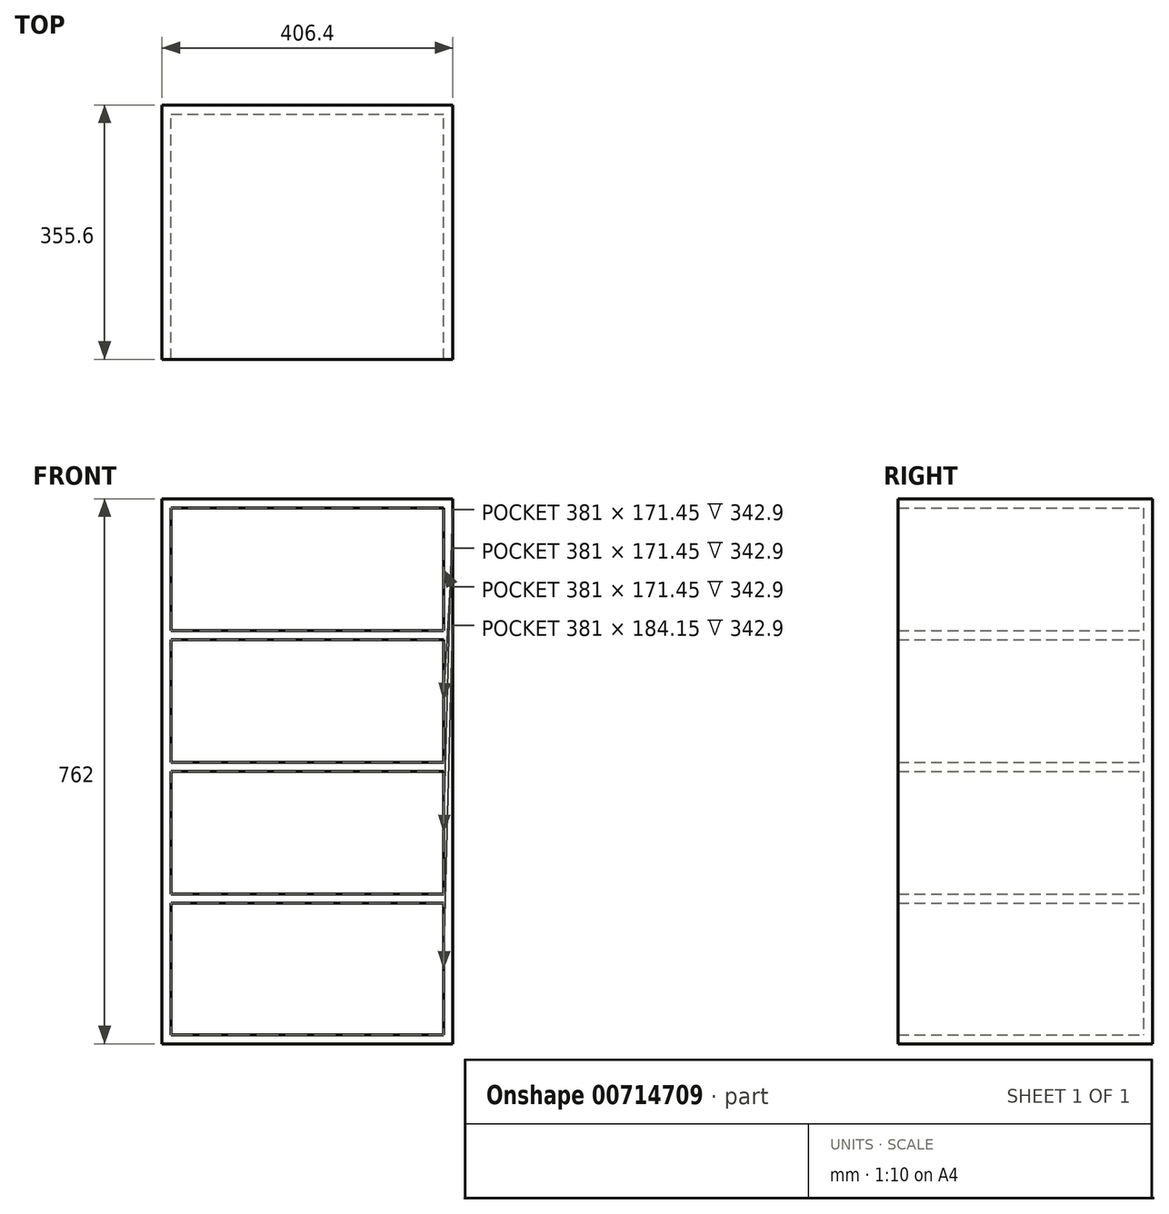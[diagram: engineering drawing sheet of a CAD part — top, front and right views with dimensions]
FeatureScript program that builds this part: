
annotation { "Feature Type Name" : "Feature", "Feature Type Description" : "" }
export const myFeature = defineFeature(function(context is Context, id is Id, definition is map)
    precondition{}
    {
        {
            var Q0;
            Q0=qCreatedBy(makeId("Front.planeOp"),FACE);
            var sketch = newSketch(context, id + "F0", { "sketchPlane" : qUnion([Q0])});
            skLineSegment(sketch, "E0.bottom", {"start": v(203.2, 381) * mm, "end": v(-203.2, 381) * mm});
            skLineSegment(sketch, "E0.top", {"start": v(203.2, -381) * mm, "end": v(-203.2, -381) * mm});
            skLineSegment(sketch, "E0.left", {"start": v(203.2, 381) * mm, "end": v(203.2, -381) * mm});
            skLineSegment(sketch, "E0.right", {"start": v(-203.2, 381) * mm, "end": v(-203.2, -381) * mm});
            skPoint(sketch, "E0.middle", {"position": v(0, 0) * mm});
            skSolve(sketch);
        }
        {
            var Q0;
            Q0 = qSketchRegion(id + "F0", true);
            extrude(context, id + "F1", {"entities" : qUnion([Q0]), "depth" : 355.6 * mm, "offsetDistance" : 25.4 * mm});
        }
        {
            var Q0;
            Q0=makeQuery(id+"F1.opExtrude","CAP_FACE",FACE,{"disambiguationData":[OSD([sQuery(id+"F0.wireOp",EDGE,"E0.bottom"),sQuery(id+"F0.wireOp",EDGE,"E0.top"),sQuery(id+"F0.wireOp",EDGE,"E0.left"),sQuery(id+"F0.wireOp",EDGE,"E0.right")])],"isStart":false});
            shell(context, id + "F2", {"entities" : qUnion([Q0]), "thickness" : 12.7 * mm});
        }
        {
            var Q0;
            Q0=makeQuery(id+"F2.opShell","OFFSET_FACE",FACE,{"disambiguationData":[OSD([sQuery(id+"F0.wireOp",EDGE,"E0.bottom"),sQuery(id+"F0.wireOp",EDGE,"E0.top"),sQuery(id+"F0.wireOp",EDGE,"E0.left"),sQuery(id+"F0.wireOp",EDGE,"E0.right")])]});
            var sketch = newSketch(context, id + "F3", { "sketchPlane" : qUnion([Q0])});
            skLineSegment(sketch, "E1", {"start": v(-190.5, 368.3) * mm, "end": v(-190.5, 196.85) * mm});
            skLineSegment(sketch, "E2", {"start": v(-190.5, 196.85) * mm, "end": v(190.5, 196.85) * mm});
            skLineSegment(sketch, "E3", {"start": v(-190.5, 196.85) * mm, "end": v(-190.5, 12.7) * mm});
            skLineSegment(sketch, "E4.top", {"start": v(-190.5, 184.15) * mm, "end": v(190.5, 184.15) * mm});
            skLineSegment(sketch, "E4.left", {"start": v(-190.5, 196.85) * mm, "end": v(-190.5, 184.15) * mm});
            skLineSegment(sketch, "E4.right", {"start": v(190.5, 196.85) * mm, "end": v(190.5, 184.15) * mm});
            skLineSegment(sketch, "E5.bottom", {"start": v(-190.5, 12.7) * mm, "end": v(190.5, 12.7) * mm});
            skLineSegment(sketch, "E5.top", {"start": v(-190.5, 0) * mm, "end": v(190.5, 0) * mm});
            skLineSegment(sketch, "E5.left", {"start": v(-190.5, 12.7) * mm, "end": v(-190.5, 0) * mm});
            skLineSegment(sketch, "E5.right", {"start": v(190.5, 12.7) * mm, "end": v(190.5, 0) * mm});
            skLineSegment(sketch, "E6", {"start": v(-190.5, 0) * mm, "end": v(-190.5, -171.45) * mm});
            skLineSegment(sketch, "E7.bottom", {"start": v(-190.5, -171.45) * mm, "end": v(190.5, -171.45) * mm});
            skLineSegment(sketch, "E7.top", {"start": v(-190.5, -184.15) * mm, "end": v(190.5, -184.15) * mm});
            skLineSegment(sketch, "E7.left", {"start": v(-190.5, -171.45) * mm, "end": v(-190.5, -184.15) * mm});
            skLineSegment(sketch, "E7.right", {"start": v(190.5, -171.45) * mm, "end": v(190.5, -184.15) * mm});
            skSolve(sketch);
        }
        {
            var Q0;
            Q0=makeQuery(id+"F3.imprint","IMPRINT",FACE,{"disambiguationData":[TD([[makeQuery(id+"F3.imprint","IMPRINT",EDGE,{"derivedFrom":sQuery(id+"F3.wireOp",EDGE,"E2")}),-1.0]])]});
            var Q1;
            Q1=makeQuery(id+"F3.imprint","IMPRINT",FACE,{"disambiguationData":[TD([[makeQuery(id+"F3.imprint","IMPRINT",EDGE,{"derivedFrom":sQuery(id+"F3.wireOp",EDGE,"E5.bottom")}),-1.0]])]});
            var Q2;
            Q2=makeQuery(id+"F3.imprint","IMPRINT",FACE,{"disambiguationData":[TD([[makeQuery(id+"F3.imprint","IMPRINT",EDGE,{"derivedFrom":sQuery(id+"F3.wireOp",EDGE,"E7.bottom")}),-1.0]])]});
            extrude(context, id + "F4", {"entities" : qUnion([Q0, Q1, Q2]), "operationType" : NewBodyOperationType.ADD, "depth" : 342.9 * mm, "offsetDistance" : 25.4 * mm});
        }
    });
